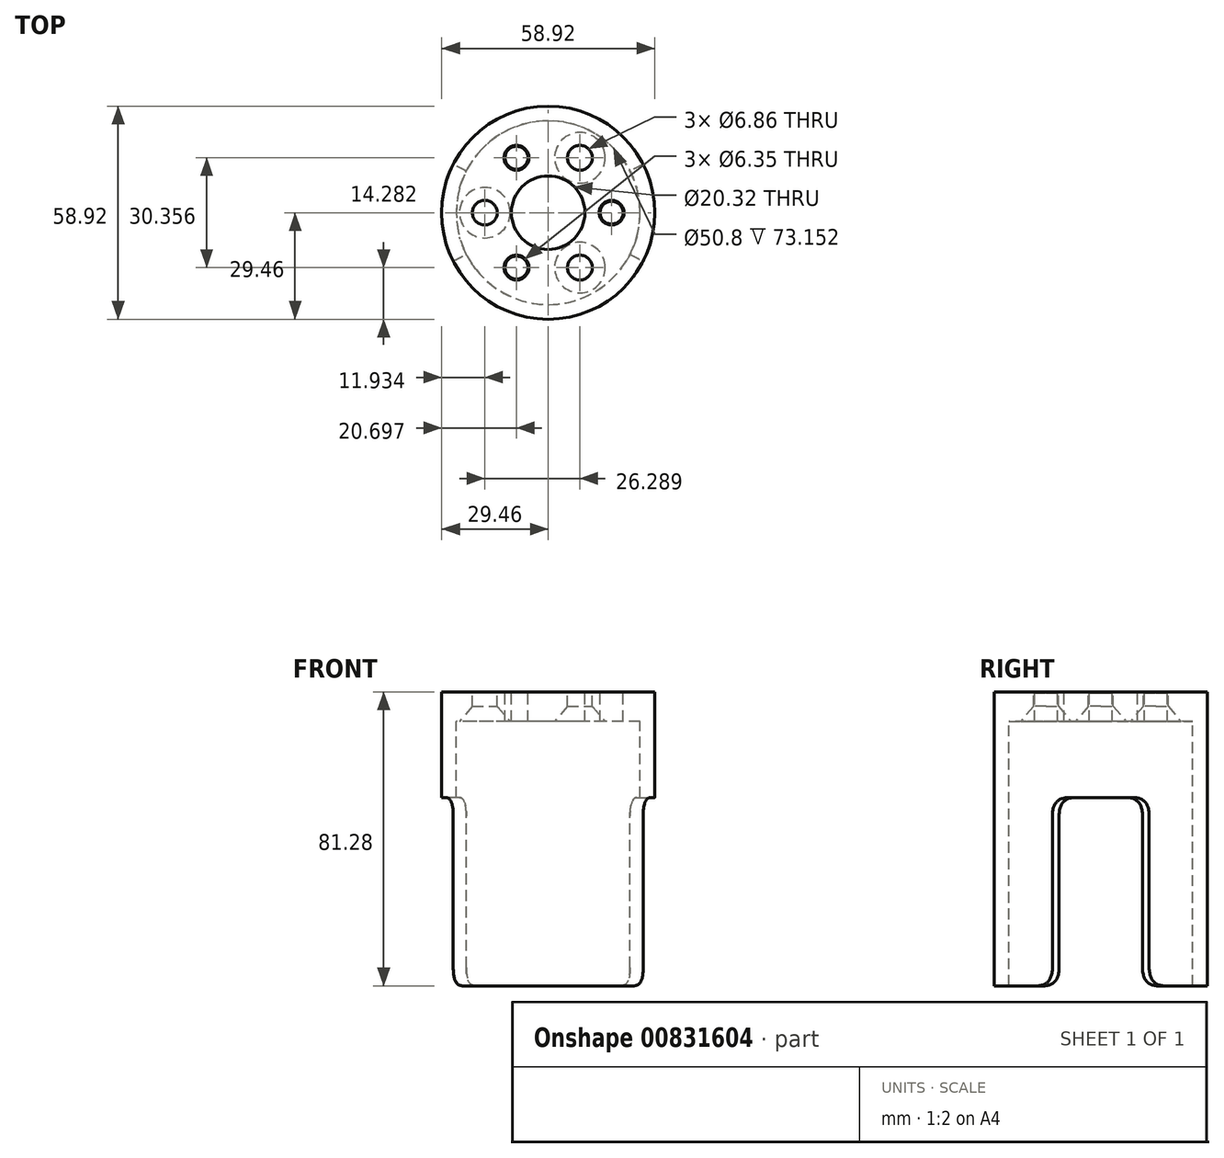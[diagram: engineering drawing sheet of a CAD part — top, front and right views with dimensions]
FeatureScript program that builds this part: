
annotation { "Feature Type Name" : "Feature", "Feature Type Description" : "" }
export const myFeature = defineFeature(function(context is Context, id is Id, definition is map)
    precondition{}
    {
        {
            var Q0;
            Q0=qCreatedBy(makeId("Top.planeOp"),FACE);
            var sketch = newSketch(context, id + "F0", { "sketchPlane" : qUnion([Q0])});
            skCircle(sketch, "E0", {"center": v(0, 0) * mm, "radius": 17.53 * mm, "construction": true});
            skCircle(sketch, "E1", {"center": v(0, 0) * mm, "radius": 10.16 * mm});
            skCircle(sketch, "E2", {"center": v(0, 0) * mm, "radius": 29.46 * mm});
            skCircle(sketch, "E3", {"center": v(17.53, 0) * mm, "radius": 3.18 * mm});
            skCircle(sketch, "E4", {"center": v(-17.53, 0) * mm, "radius": 3.43 * mm});
            skCircle(sketch, "E5.1.0", {"center": v(-8.76, 15.18) * mm, "radius": 3.18 * mm});
            skCircle(sketch, "E5.2.0", {"center": v(-8.76, -15.18) * mm, "radius": 3.18 * mm});
            skCircle(sketch, "E6.1.0", {"center": v(8.76, -15.18) * mm, "radius": 3.43 * mm});
            skCircle(sketch, "E6.2.0", {"center": v(8.76, 15.18) * mm, "radius": 3.43 * mm});
            skSolve(sketch);
        }
        {
            var Q0;
            Q0=makeQuery(id+"F0.imprint","IMPRINT",FACE,{"disambiguationData":[TD([[makeQuery(id+"F0.imprint","IMPRINT",EDGE,{"derivedFrom":sQuery(id+"F0.wireOp",EDGE,"E1")}),-1.0]])]});
            extrude(context, id + "F1", {"entities" : qUnion([Q0]), "oppositeDirection" : true, "depth" : 81.28 * mm, "offsetDistance" : 25.4 * mm});
        }
        {
            var Q0;
            Q0=qCreatedBy(makeId("Top.planeOp"),FACE);
            cPlane(context, id + "F2", {"entities" : qUnion([Q0]), "cplaneType" : CPlaneType.OFFSET, "offset" : 8.13 * mm, "oppositeDirection" : true, "width" : 152.4 * mm, "height" : 152.4 * mm});
        }
        {
            var Q0;
            Q0=qCreatedBy(id+"F2.planeOp",FACE);
            var sketch = newSketch(context, id + "F3", { "sketchPlane" : qUnion([Q0])});
            skCircle(sketch, "E7", {"center": v(0, 0) * mm, "radius": 25.4 * mm});
            skSolve(sketch);
        }
        {
            var Q0;
            Q0=makeQuery(id+"F3.imprint","IMPRINT",FACE,{"disambiguationData":[TD([[makeQuery(id+"F3.imprint","IMPRINT",EDGE,{"derivedFrom":sQuery(id+"F3.wireOp",EDGE,"E7")}),1.0]])]});
            extrude(context, id + "F4", {"entities" : qUnion([Q0]), "operationType" : NewBodyOperationType.REMOVE, "endBound" : BoundingType.THROUGH_ALL, "oppositeDirection" : true, "depth" : 25.4 * mm, "offsetDistance" : 25.4 * mm});
        }
        {
            var Q0;
            Q0=qCreatedBy(makeId("Top.planeOp"),FACE);
            cPlane(context, id + "F5", {"entities" : qUnion([Q0]), "cplaneType" : CPlaneType.OFFSET, "offset" : 29.2 * mm, "oppositeDirection" : true, "width" : 152.4 * mm, "height" : 152.4 * mm});
        }
        {
            var Q0;
            Q0=qCreatedBy(id+"F5.planeOp",FACE);
            var sketch = newSketch(context, id + "F6", { "sketchPlane" : qUnion([Q0])});
            skCircle(sketch, "E8", {"center": v(0, 0) * mm, "radius": 29.46 * mm, "construction": true});
            skCircle(sketch, "E9", {"center": v(0, 0) * mm, "radius": 25.4 * mm, "construction": true});
            skPoint(sketch, "E10", {"position": v(-22.63, 11.53) * mm});
            skPoint(sketch, "E11", {"position": v(-22.63, -11.53) * mm});
            skLineSegment(sketch, "E12", {"start": v(-26.25, 13.38) * mm, "end": v(26.25, -13.38) * mm, "construction": true});
            skLineSegment(sketch, "E13", {"start": v(26.25, 13.38) * mm, "end": v(-26.25, -13.38) * mm, "construction": true});
            skLineSegment(sketch, "E14", {"start": v(-22.63, 11.53) * mm, "end": v(-22.63, -11.53) * mm});
            skLineSegment(sketch, "E15", {"start": v(-22.63, 11.53) * mm, "end": v(-26.25, 13.38) * mm});
            skLineSegment(sketch, "E16", {"start": v(-22.63, -11.53) * mm, "end": v(-26.25, -13.38) * mm});
            skPoint(sketch, "E17", {"position": v(-29.46, 0) * mm});
            skArc(sketch, "E18", {"start": v(-26.25, 13.38) * mm, "mid": v(-29.46, 0) * mm, "end": v(-26.25, -13.38) * mm});
            skPoint(sketch, "E19", {"position": v(22.63, 11.53) * mm});
            skPoint(sketch, "E20", {"position": v(22.63, -11.53) * mm});
            skLineSegment(sketch, "E21", {"start": v(26.25, 13.38) * mm, "end": v(22.63, 11.53) * mm});
            skLineSegment(sketch, "E22", {"start": v(22.63, 11.53) * mm, "end": v(22.63, -11.53) * mm});
            skLineSegment(sketch, "E23", {"start": v(22.63, -11.53) * mm, "end": v(26.25, -13.38) * mm});
            skPoint(sketch, "E24", {"position": v(29.46, 0) * mm});
            skArc(sketch, "E25", {"start": v(26.25, -13.38) * mm, "mid": v(29.46, 0) * mm, "end": v(26.25, 13.38) * mm});
            skSolve(sketch);
        }
        {
            var Q0;
            Q0=qSketchRegion(id+"F6",true);
            extrude(context, id + "F7", {"entities" : qUnion([Q0]), "operationType" : NewBodyOperationType.REMOVE, "endBound" : BoundingType.THROUGH_ALL, "oppositeDirection" : true, "depth" : 25.4 * mm, "offsetDistance" : 25.4 * mm});
        }
        {
            var Q0;
            Q0=makeQuery(id+"F7.boolean.opBoolean","INTERSECT",EDGE,{"derivedFrom":[makeQuery(id+"F1.opExtrude","CAP_FACE",FACE,{"disambiguationData":[OSD([sQuery(id+"F0.wireOp",EDGE,"E1"),sQuery(id+"F0.wireOp",EDGE,"E2"),sQuery(id+"F0.wireOp",EDGE,"E3"),sQuery(id+"F0.wireOp",EDGE,"E4"),sQuery(id+"F0.wireOp",EDGE,"E5.1.0"),sQuery(id+"F0.wireOp",EDGE,"E5.2.0"),sQuery(id+"F0.wireOp",EDGE,"E6.1.0"),sQuery(id+"F0.wireOp",EDGE,"E6.2.0")])],"isStart":false}),makeQuery(id+"F7.opExtrude","SWEPT_FACE",FACE,{"disambiguationData":[OSD([sQuery(id+"F6.wireOp",EDGE,"E23")])]})]});
            var Q1;
            Q1=makeQuery(id+"F7.boolean.opBoolean","INTERSECT",EDGE,{"derivedFrom":[makeQuery(id+"F1.opExtrude","CAP_FACE",FACE,{"disambiguationData":[OSD([sQuery(id+"F0.wireOp",EDGE,"E1"),sQuery(id+"F0.wireOp",EDGE,"E2"),sQuery(id+"F0.wireOp",EDGE,"E3"),sQuery(id+"F0.wireOp",EDGE,"E4"),sQuery(id+"F0.wireOp",EDGE,"E5.1.0"),sQuery(id+"F0.wireOp",EDGE,"E5.2.0"),sQuery(id+"F0.wireOp",EDGE,"E6.1.0"),sQuery(id+"F0.wireOp",EDGE,"E6.2.0")])],"isStart":false}),makeQuery(id+"F7.opExtrude","SWEPT_FACE",FACE,{"disambiguationData":[OSD([sQuery(id+"F6.wireOp",EDGE,"E21")])]})]});
            var Q2;
            Q2=makeQuery(id+"F7.boolean.opBoolean","INTERSECT",EDGE,{"derivedFrom":[makeQuery(id+"F1.opExtrude","CAP_FACE",FACE,{"disambiguationData":[OSD([sQuery(id+"F0.wireOp",EDGE,"E1"),sQuery(id+"F0.wireOp",EDGE,"E2"),sQuery(id+"F0.wireOp",EDGE,"E3"),sQuery(id+"F0.wireOp",EDGE,"E4"),sQuery(id+"F0.wireOp",EDGE,"E5.1.0"),sQuery(id+"F0.wireOp",EDGE,"E5.2.0"),sQuery(id+"F0.wireOp",EDGE,"E6.1.0"),sQuery(id+"F0.wireOp",EDGE,"E6.2.0")])],"isStart":false}),makeQuery(id+"F7.opExtrude","SWEPT_FACE",FACE,{"disambiguationData":[OSD([sQuery(id+"F6.wireOp",EDGE,"E15")])]})]});
            var Q3;
            Q3=makeQuery(id+"F7.boolean.opBoolean","INTERSECT",EDGE,{"derivedFrom":[makeQuery(id+"F1.opExtrude","CAP_FACE",FACE,{"disambiguationData":[OSD([sQuery(id+"F0.wireOp",EDGE,"E1"),sQuery(id+"F0.wireOp",EDGE,"E2"),sQuery(id+"F0.wireOp",EDGE,"E3"),sQuery(id+"F0.wireOp",EDGE,"E4"),sQuery(id+"F0.wireOp",EDGE,"E5.1.0"),sQuery(id+"F0.wireOp",EDGE,"E5.2.0"),sQuery(id+"F0.wireOp",EDGE,"E6.1.0"),sQuery(id+"F0.wireOp",EDGE,"E6.2.0")])],"isStart":false}),makeQuery(id+"F7.opExtrude","SWEPT_FACE",FACE,{"disambiguationData":[OSD([sQuery(id+"F6.wireOp",EDGE,"E16")])]})]});
            fillet(context, id + "F8", {"entities" : qUnion([Q0, Q1, Q2, Q3]), "radius" : 5.08 * mm, "tangentPropagation" : true, "rho" : 0.5, "crossSection" : FilletCrossSection.CONIC, "allowEdgeOverflow" : false});
        }
        {
            var Q0;
            Q0=makeQuery(id+"F7.boolean.opBoolean","COPY",EDGE,{"derivedFrom":makeQuery(id+"F7.opExtrude","CAP_EDGE",EDGE,{"disambiguationData":[OSD([sQuery(id+"F6.wireOp",EDGE,"E16")])],"isStart":true})});
            var Q1;
            Q1=makeQuery(id+"F7.boolean.opBoolean","COPY",EDGE,{"derivedFrom":makeQuery(id+"F7.opExtrude","CAP_EDGE",EDGE,{"disambiguationData":[OSD([sQuery(id+"F6.wireOp",EDGE,"E15")])],"isStart":true})});
            var Q2;
            Q2=makeQuery(id+"F7.boolean.opBoolean","COPY",EDGE,{"derivedFrom":makeQuery(id+"F7.opExtrude","CAP_EDGE",EDGE,{"disambiguationData":[OSD([sQuery(id+"F6.wireOp",EDGE,"E23")])],"isStart":true})});
            var Q3;
            Q3=makeQuery(id+"F7.boolean.opBoolean","COPY",EDGE,{"derivedFrom":makeQuery(id+"F7.opExtrude","CAP_EDGE",EDGE,{"disambiguationData":[OSD([sQuery(id+"F6.wireOp",EDGE,"E21")])],"isStart":true})});
            fillet(context, id + "F9", {"entities" : qUnion([Q0, Q1, Q2, Q3]), "radius" : 5.08 * mm, "tangentPropagation" : true, "rho" : 0.5, "crossSection" : FilletCrossSection.CONIC, "allowEdgeOverflow" : false});
        }
        {
            var Q0;
            Q0=qCreatedBy(makeId("Top.planeOp"),FACE);
            var sketch = newSketch(context, id + "F10", { "sketchPlane" : qUnion([Q0])});
            skCircle(sketch, "E26", {"center": v(0, 0) * mm, "radius": 17.53 * mm, "construction": true});
            skCircle(sketch, "E27", {"center": v(17.53, 0) * mm, "radius": 3.43 * mm});
            skCircle(sketch, "E28.1.0", {"center": v(-8.76, 15.18) * mm, "radius": 3.43 * mm});
            skCircle(sketch, "E28.2.0", {"center": v(-8.76, -15.18) * mm, "radius": 3.43 * mm});
            skSolve(sketch);
        }
        {
            var Q0;
            Q0=makeQuery(id+"F10.imprint","IMPRINT",FACE,{"disambiguationData":[TD([[makeQuery(id+"F10.imprint","IMPRINT",EDGE,{"derivedFrom":sQuery(id+"F10.wireOp",EDGE,"E27")}),1.0]])]});
            var Q1;
            Q1=makeQuery(id+"F10.imprint","IMPRINT",FACE,{"disambiguationData":[TD([[makeQuery(id+"F10.imprint","IMPRINT",EDGE,{"derivedFrom":sQuery(id+"F10.wireOp",EDGE,"E28.1.0")}),1.0]])]});
            var Q2;
            Q2=makeQuery(id+"F10.imprint","IMPRINT",FACE,{"disambiguationData":[TD([[makeQuery(id+"F10.imprint","IMPRINT",EDGE,{"derivedFrom":sQuery(id+"F10.wireOp",EDGE,"E28.2.0")}),1.0]])]});
            extrude(context, id + "F11", {"entities" : qUnion([Q0, Q1, Q2]), "operationType" : NewBodyOperationType.REMOVE, "oppositeDirection" : true, "depth" : 2.54 * mm, "offsetDistance" : 25.4 * mm, "hasDraft" : true, "draftAngle" : 45 * degree, "draftPullDirection" : true});
        }
        {
            var Q0;
            Q0=qCreatedBy(id+"F2.planeOp",FACE);
            var sketch = newSketch(context, id + "F12", { "sketchPlane" : qUnion([Q0])});
            skCircle(sketch, "E29", {"center": v(0, 0) * mm, "radius": 17.53 * mm, "construction": true});
            skCircle(sketch, "E30", {"center": v(-17.53, 0) * mm, "radius": 6.99 * mm});
            skCircle(sketch, "E31.1.0", {"center": v(8.76, -15.18) * mm, "radius": 6.99 * mm});
            skCircle(sketch, "E31.2.0", {"center": v(8.76, 15.18) * mm, "radius": 6.99 * mm});
            skSolve(sketch);
        }
        {
            var Q0;
            Q0=makeQuery(id+"F12.imprint","IMPRINT",FACE,{"disambiguationData":[TD([[makeQuery(id+"F12.imprint","IMPRINT",EDGE,{"derivedFrom":sQuery(id+"F12.wireOp",EDGE,"E30")}),1.0]])]});
            var Q1;
            Q1=makeQuery(id+"F12.imprint","IMPRINT",FACE,{"disambiguationData":[TD([[makeQuery(id+"F12.imprint","IMPRINT",EDGE,{"derivedFrom":sQuery(id+"F12.wireOp",EDGE,"E31.1.0")}),1.0]])]});
            var Q2;
            Q2=makeQuery(id+"F12.imprint","IMPRINT",FACE,{"disambiguationData":[TD([[makeQuery(id+"F12.imprint","IMPRINT",EDGE,{"derivedFrom":sQuery(id+"F12.wireOp",EDGE,"E31.2.0")}),1.0]])]});
            extrude(context, id + "F13", {"entities" : qUnion([Q0, Q1, Q2]), "operationType" : NewBodyOperationType.REMOVE, "endBound" : BoundingType.THROUGH_ALL, "depth" : 6.35 * mm, "offsetDistance" : 25.4 * mm, "hasDraft" : true, "draftAngle" : 41 * degree, "draftPullDirection" : true});
        }
    });
